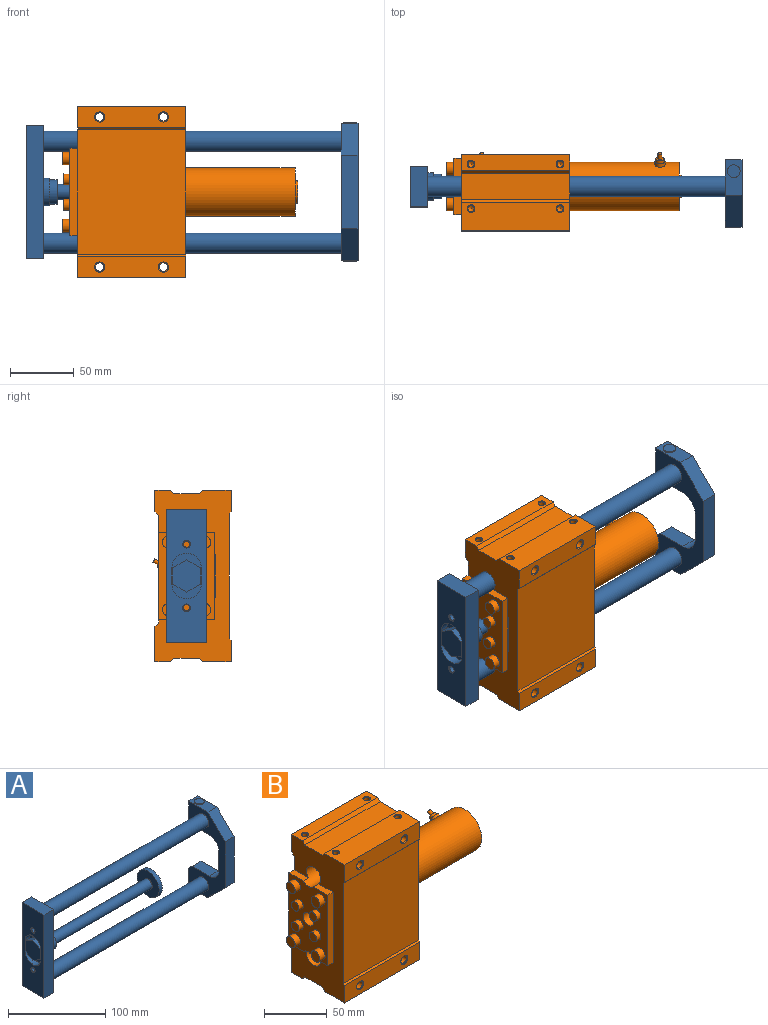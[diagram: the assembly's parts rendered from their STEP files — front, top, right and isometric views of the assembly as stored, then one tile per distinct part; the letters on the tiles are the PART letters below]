
ASSEMBLY  parts=2 mates=1
PART A: 58 faces, bbox 261x53x110 mm
  f0: plane 28x13mm, normal (0,0,1), area 285.5mm2, adj f1,f2,f11,f49,f55
  f1: plane 23x13mm, normal (0,1,0), area 299mm2, adj f0,f2,f49,f53
  f2: plane 108x53mm, normal (1,0,0), area 2468mm2, adj f0,f1,f3,f4,f5,f6,f7,f8
  f3: cylinder r=8mm len=16mm, axis (1,0,0), area 0.5mm2, adj f2,f22
  f4: plane 24x13mm, normal (0,1,0), area 312mm2, adj f2,f49,f51,f52
  f5: plane 25x13mm, normal (0,0,-1), area 325mm2, adj f2,f49,f52,f53
  f6: plane 25x13mm, normal (0,0,1), area 325mm2, adj f2,f49,f50,f51
  f7: plane 23x13mm, normal (0,1,0), area 299mm2, adj f2,f8,f49,f50
  f8: plane 28x13mm, normal (0,0,-1), area 285.5mm2, adj f2,f7,f9,f49,f56
  f9: plane 25x25mm, normal (0,-0.71,-0.71), area 459.6mm2, adj f2,f8,f10,f49
  f10: plane 58x13mm, normal (0,-1,0), area 754mm2, adj f2,f9,f11,f49
  f11: plane 25x25mm, normal (0,-0.71,0.71), area 459.6mm2, adj f0,f2,f10,f49
  f12: plane 32x32mm, normal (1,0,0), area 804.2mm2, adj f13
  f13: cylinder r=16mm len=32mm, axis (-1,0,0), area 502.7mm2, adj f12,f14
  f14: plane 32x32mm, normal (-1,0,0), area 691.2mm2, adj f13,f15
  f15: cylinder r=6mm len=143.23mm, axis (-1,0,0), area 5399.6mm2, adj f14,f16
  f16: plane 19.6x19.6mm, normal (1,0,0), area 188.6mm2, adj f15,f17
  f17: cylinder r=9.8mm len=19.6mm, axis (-1,0,0), area 369.5mm2, adj f16,f18
  f18: plane 22x22mm, normal (1,0,0), area 78.4mm2, adj f17,f19
  f19: cylinder r=11mm len=22mm, axis (-1,0,0), area 311mm2, adj f18,f41
  f20: plane 16x16mm, normal (1,0,0), area 201.1mm2, adj f48
  f21: cylinder r=8mm len=234mm, axis (1,0,0), area 11762.1mm2, adj f41,f49
  f22: plane 16x16mm, normal (1,0,0), area 201.1mm2, adj f3
  f23: cylinder r=8mm len=234mm, axis (1,0,0), area 11762.1mm2, adj f41,f49
  f24: plane 36x23mm, normal (-1,0,0), area 295.3mm2, adj f25,f26,f27,f28,f29,f30,f31,f32
  f25: plane 11x7mm, normal (0,0.5,0.87), area 88.9mm2, adj f24,f26,f30,f47
  f26: plane 12.7x7mm, normal (0,1,0), area 88.9mm2, adj f24,f25,f27,f47
  f27: plane 11x7mm, normal (0,0.5,-0.87), area 88.9mm2, adj f24,f26,f28,f47
  f28: plane 11x7mm, normal (0,-0.5,-0.87), area 88.9mm2, adj f24,f27,f29,f47
  f29: plane 12.7x7mm, normal (0,-1,0), area 88.9mm2, adj f24,f28,f30,f47
  f30: plane 11x7mm, normal (0,-0.5,0.87), area 88.9mm2, adj f24,f25,f29,f47
  f31: cylinder r=11.5mm len=23mm, axis (1,0,0), area 252.9mm2, adj f24,f32,f34,f42
  f32: plane 13x7mm, normal (0,1,0), area 91mm2, adj f24,f31,f33,f42
  f33: cylinder r=11.5mm len=23mm, axis (1,0,0), area 252.9mm2, adj f24,f32,f34,f42
  f34: plane 13x7mm, normal (0,-1,0), area 91mm2, adj f24,f31,f33,f42
  f35: cone r=2.46mm half-angle=45deg, axis (1,0,0), area 13.1mm2, adj f36,f41
  f36: cylinder r=2.46mm len=12.92mm, axis (-1,0,0), area 199.5mm2, adj f35,f37
  f37: cone r=3mm half-angle=45deg, axis (-1,0,0), area 13.1mm2, adj f36,f42
  f38: cone r=2.46mm half-angle=45deg, axis (1,0,0), area 13.1mm2, adj f39,f41
  f39: cylinder r=2.46mm len=12.92mm, axis (-1,0,0), area 199.5mm2, adj f38,f40
  f40: cone r=3mm half-angle=45deg, axis (-1,0,0), area 13.1mm2, adj f39,f42
  f41: plane 105x32mm, normal (1,0,0), area 2521.2mm2, adj f19,f21,f23,f35,f38,f43,f44,f45
  f42: plane 105x32mm, normal (-1,0,0), area 2589mm2, adj f31,f32,f33,f34,f37,f40,f43,f44
  f43: plane 105x14mm, normal (0,1,0), area 1470mm2, adj f41,f42,f44,f46
  f44: plane 32x14mm, normal (0,0,-1), area 448mm2, adj f41,f42,f43,f45
  f45: plane 105x14mm, normal (0,-1,0), area 1470mm2, adj f41,f42,f44,f46
  f46: plane 32x14mm, normal (0,0,1), area 448mm2, adj f41,f42,f43,f45
  f47: plane 25.4x22mm, normal (-1,0,0), area 419.2mm2, adj f25,f26,f27,f28,f29,f30
  f48: cylinder r=8mm len=16mm, axis (1,0,0), area 0.5mm2, adj f2,f20
  f49: plane 108x53mm, normal (-1,0,0), area 2468mm2, adj f0,f1,f4,f5,f6,f7,f8,f9
  f50: plane 13x5mm, normal (0,0.71,0.71), area 91.9mm2, adj f2,f6,f7,f49
  f51: cylinder r=14mm len=14mm, axis (1,0,0), area 285.9mm2, adj f2,f4,f6,f49
  f52: cylinder r=14mm len=14mm, axis (1,0,0), area 285.9mm2, adj f2,f4,f5,f49
  f53: plane 13x5mm, normal (0,0.71,-0.71), area 91.9mm2, adj f1,f2,f5,f49
  f54: plane 10x10mm, normal (0,0,1), area 78.5mm2, adj f55
  f55: cylinder r=5mm len=10mm, axis (0,0,1), area 31.4mm2, adj f0,f54
  f56: cylinder r=5mm len=10mm, axis (0,0,1), area 31.4mm2, adj f8,f57
  f57: plane 10x10mm, normal (0,0,-1), area 78.5mm2, adj f56
PART B: 128 faces, bbox 185x61.5x135 mm
  f0: cone r=866.03mm half-angle=60deg, axis (0,0,-1), area 21.9mm2, adj f1
  f1: cylinder r=2.46mm len=11.46mm, axis (0,0,1), area 177mm2, adj f0,f127
  f2: cone r=2.46mm half-angle=45deg, axis (0,0,-1), area 13.1mm2, adj f43,f103
  f3: cylinder r=19mm len=171mm, axis (1,0,0), area 20162.4mm2, adj f5,f8,f11,f18,f53,f60
  f4: plane 85x12.5mm, normal (0,0,1), area 1006mm2, adj f23,f24,f27,f52,f119,f122
  f5: cylinder r=4.05mm len=8.58mm, axis (0,-0.91,-0.42), area 69.1mm2, adj f3,f59
  f6: plane 18x18mm, normal (1,0,0), area 254.5mm2, adj f7
  f7: cylinder r=9mm len=18mm, axis (1,0,0), area 113.1mm2, adj f6,f18
  f8: cone r=4.28mm half-angle=45deg, axis (0,0.98,-0.17), area 12.2mm2, adj f3,f9
  f9: cylinder r=4.28mm len=9.2mm, axis (0,-0.98,0.17), area 118.9mm2, adj f8,f10
  f10: cone r=866.03mm half-angle=60deg, axis (0,0.98,-0.17), area 66.5mm2, adj f9
  f11: cone r=4.28mm half-angle=45deg, axis (0,0.98,-0.17), area 12.2mm2, adj f3,f12
  f12: cylinder r=4.28mm len=9.2mm, axis (0,-0.98,0.17), area 118.9mm2, adj f11,f13
  f13: cone r=866.03mm half-angle=60deg, axis (0,0.98,-0.17), area 66.5mm2, adj f12
  f14: plane 32x32mm, normal (-1,0,0), area 804.2mm2, adj f15
  f15: cylinder r=16mm len=105mm, axis (-1,0,0), area 10555.8mm2, adj f14,f16
  f16: plane 32x32mm, normal (1,0,0), area 691.2mm2, adj f15,f17
  f17: cylinder r=6mm len=27.73mm, axis (-1,0,0), area 1045.3mm2, adj f16,f62
  f18: plane 38x38mm, normal (1,0,0), area 879.6mm2, adj f3,f7
  f19: plane 69x6mm, normal (0,-1,0), area 414mm2, adj f20,f21,f24,f60,f62
  f20: plane 16.19x6mm, normal (0,0,-1), area 97.1mm2, adj f19,f24,f26,f62
  f21: plane 16.19x6mm, normal (0,0,1), area 97.1mm2, adj f19,f24,f25,f62
  f22: plane 16.19x6mm, normal (0,0,1), area 97.1mm2, adj f24,f25,f29,f62
  f23: plane 135x60mm, normal (1,0,0), area 5183.7mm2, adj f4,f25,f26,f27,f28,f29,f30,f31
  f24: plane 135x60mm, normal (-1,0,0), area 4137.7mm2, adj f4,f19,f20,f21,f22,f25,f26,f27
  f25: cylinder r=8mm len=91mm, axis (1,0,0), area 4350.6mm2, adj f21,f22,f23,f24,f62
  f26: cylinder r=8mm len=91mm, axis (1,0,0), area 4350.6mm2, adj f20,f23,f24,f61,f62
  f27: plane 85x17mm, normal (0,1,0), area 1254.9mm2, adj f4,f23,f24,f28,f84,f90
  f28: plane 85x3mm, normal (0,0.71,-0.71), area 360.6mm2, adj f23,f24,f27,f29
  f29: plane 91x84.5mm, normal (0,1,0), area 3006.5mm2, adj f22,f23,f24,f28,f30,f36,f37,f60
  f30: plane 85x5mm, normal (0,0.71,-0.71), area 601mm2, adj f23,f29,f31,f60
  f31: plane 85x33.5mm, normal (0,0,-1), area 2847.5mm2, adj f23,f30,f32,f60
  f32: cylinder r=6mm len=85mm, axis (1,0,0), area 801.1mm2, adj f23,f24,f31,f33,f60
  f33: plane 85x32mm, normal (0,1,0), area 2720mm2, adj f23,f24,f32,f34
  f34: cylinder r=6mm len=85mm, axis (1,0,0), area 801.1mm2, adj f23,f24,f33,f35,f60
  f35: plane 85x33.5mm, normal (0,0,1), area 2847.5mm2, adj f23,f34,f36,f60
  f36: plane 85x5mm, normal (0,0.71,0.71), area 601mm2, adj f23,f29,f35,f60
  f37: plane 85x3mm, normal (0,0.71,0.71), area 360.6mm2, adj f23,f24,f29,f38
  f38: plane 85x27.5mm, normal (0,1,0), area 2147.4mm2, adj f23,f24,f37,f39,f96,f102
  f39: plane 85x12.5mm, normal (0,0,-1), area 1006mm2, adj f23,f24,f38,f40,f105,f108
  f40: plane 85x3mm, normal (0,-0.77,-0.64), area 332.9mm2, adj f23,f24,f39,f41
  f41: plane 85x19.97mm, normal (0,0,-1), area 1697.1mm2, adj f23,f24,f40,f42
  f42: plane 85x3mm, normal (0,0.77,-0.64), area 332.9mm2, adj f23,f24,f41,f43
  f43: plane 85x22.5mm, normal (0,0,-1), area 1856mm2, adj f2,f23,f24,f42,f44,f127
  f44: plane 85x17mm, normal (0,-1,0), area 1344.5mm2, adj f23,f24,f43,f45,f91,f97
  f45: plane 85x1.5mm, normal (0,-0.71,0.71), area 180.3mm2, adj f23,f24,f44,f46
  f46: plane 98x85mm, normal (0,-1,0), area 8330mm2, adj f23,f24,f45,f47
  f47: plane 85x1.5mm, normal (0,-0.71,-0.71), area 180.3mm2, adj f23,f24,f46,f48
  f48: plane 85x17mm, normal (0,-1,0), area 1344.5mm2, adj f23,f24,f47,f49,f79,f85
  f49: plane 85x22.5mm, normal (0,0,1), area 1856mm2, adj f23,f24,f48,f50,f113,f116
  f50: plane 85x3mm, normal (0,0.77,0.64), area 332.9mm2, adj f23,f24,f49,f51
  f51: plane 85x19.97mm, normal (0,0,1), area 1697.1mm2, adj f23,f24,f50,f52
  f52: plane 85x3mm, normal (0,-0.77,0.64), area 332.9mm2, adj f4,f23,f24,f51
  f53: cylinder r=4.05mm len=8.58mm, axis (0,-0.91,-0.42), area 69.1mm2, adj f3,f54
  f54: plane 8.1x7.34mm, normal (0,0.91,0.42), area 14.1mm2, adj f53,f126
  f55: plane 3.2x2.9mm, normal (0,0.91,0.42), area 8mm2, adj f56
  f56: cylinder r=1.6mm len=5.52mm, axis (0,-0.91,-0.42), area 46.2mm2, adj f55,f57
  f57: plane 6.9x6.25mm, normal (0,0.91,0.42), area 29.4mm2, adj f56,f58
  f58: cylinder r=3.45mm len=7.27mm, axis (0,-0.91,-0.42), area 52mm2, adj f57,f59
  f59: plane 8.1x7.34mm, normal (0,0.91,0.42), area 14.1mm2, adj f5,f58
  f60: plane 54x44mm, normal (1,0,0), area 815.8mm2, adj f3,f19,f29,f30,f31,f32,f34,f35
  f61: plane 16.19x6mm, normal (0,0,-1), area 97.1mm2, adj f24,f26,f29,f62
  f62: plane 69x44mm, normal (-1,0,0), area 2341.6mm2, adj f17,f19,f20,f21,f22,f25,f26,f29
  f63: plane 10x10mm, normal (-1,0,0), area 78.5mm2, adj f66
  f64: cylinder r=5mm len=10mm, axis (-1,0,0), area 188.5mm2, adj f62,f65
  f65: plane 10x10mm, normal (-1,0,0), area 78.5mm2, adj f64
  f66: cylinder r=5mm len=10mm, axis (-1,0,0), area 188.5mm2, adj f62,f63
  f67: plane 10x10mm, normal (-1,0,0), area 78.5mm2, adj f68
  f68: cylinder r=5mm len=10mm, axis (-1,0,0), area 188.5mm2, adj f62,f67
  f69: plane 10x10mm, normal (-1,0,0), area 78.5mm2, adj f70
  f70: cylinder r=5mm len=10mm, axis (-1,0,0), area 188.5mm2, adj f62,f69
  f71: plane 8.5x8.5mm, normal (-1,0,0), area 56.7mm2, adj f72
  f72: cylinder r=4.25mm len=8.5mm, axis (-1,0,0), area 133.5mm2, adj f62,f71
  f73: plane 8.5x8.5mm, normal (-1,0,0), area 56.7mm2, adj f74
  f74: cylinder r=4.25mm len=8.5mm, axis (-1,0,0), area 133.5mm2, adj f62,f73
  f75: plane 8.5x8.5mm, normal (-1,0,0), area 56.7mm2, adj f76
  f76: cylinder r=4.25mm len=8.5mm, axis (-1,0,0), area 133.5mm2, adj f62,f75
  f77: plane 8.5x8.5mm, normal (-1,0,0), area 56.7mm2, adj f78
  f78: cylinder r=4.25mm len=8.5mm, axis (-1,0,0), area 133.5mm2, adj f62,f77
  f79: cone r=4mm half-angle=45deg, axis (0,-1,0), area 22mm2, adj f48,f80
  f80: cylinder r=3.32mm len=13.32mm, axis (0,-1,0), area 278.2mm2, adj f79,f81
  f81: plane 6.8x6.8mm, normal (0,1,0), area 1.6mm2, adj f80,f82
  f82: cylinder r=3.4mm len=38mm, axis (0,-1,0), area 811.8mm2, adj f81,f83
  f83: plane 11x11mm, normal (0,1,0), area 58.7mm2, adj f82,f84
  f84: cylinder r=5.5mm len=11mm, axis (0,-1,0), area 276.5mm2, adj f27,f83
  f85: cone r=4mm half-angle=45deg, axis (0,-1,0), area 22mm2, adj f48,f86
  f86: cylinder r=3.32mm len=13.32mm, axis (0,-1,0), area 278.2mm2, adj f85,f87
  f87: plane 6.8x6.8mm, normal (0,1,0), area 1.6mm2, adj f86,f88
  f88: cylinder r=3.4mm len=38mm, axis (0,-1,0), area 811.8mm2, adj f87,f89
  f89: plane 11x11mm, normal (0,1,0), area 58.7mm2, adj f88,f90
  f90: cylinder r=5.5mm len=11mm, axis (0,-1,0), area 276.5mm2, adj f27,f89
  f91: cone r=4mm half-angle=45deg, axis (0,-1,0), area 22mm2, adj f44,f92
  f92: cylinder r=3.32mm len=13.32mm, axis (0,-1,0), area 278.2mm2, adj f91,f93
  f93: plane 6.8x6.8mm, normal (0,1,0), area 1.6mm2, adj f92,f94
  f94: cylinder r=3.4mm len=38mm, axis (0,-1,0), area 811.8mm2, adj f93,f95
  f95: plane 11x11mm, normal (0,1,0), area 58.7mm2, adj f94,f96
  f96: cylinder r=5.5mm len=11mm, axis (0,-1,0), area 276.5mm2, adj f38,f95
  f97: cone r=4mm half-angle=45deg, axis (0,-1,0), area 22mm2, adj f44,f98
  f98: cylinder r=3.32mm len=13.32mm, axis (0,-1,0), area 278.2mm2, adj f97,f99
  f99: plane 6.8x6.8mm, normal (0,1,0), area 1.6mm2, adj f98,f100
  f100: cylinder r=3.4mm len=38mm, axis (0,-1,0), area 811.8mm2, adj f99,f101
  f101: plane 11x11mm, normal (0,1,0), area 58.7mm2, adj f100,f102
  f102: cylinder r=5.5mm len=11mm, axis (0,-1,0), area 276.5mm2, adj f38,f101
  f103: cylinder r=2.46mm len=11.46mm, axis (0,0,1), area 177mm2, adj f2,f104
  f104: cone r=866.03mm half-angle=60deg, axis (0,0,-1), area 21.9mm2, adj f103
  f105: cone r=2.46mm half-angle=45deg, axis (0,0,-1), area 13.1mm2, adj f39,f106
  f106: cylinder r=2.46mm len=11.46mm, axis (0,0,1), area 177mm2, adj f105,f107
  f107: cone r=866.03mm half-angle=60deg, axis (0,0,-1), area 21.9mm2, adj f106
  f108: cone r=2.46mm half-angle=45deg, axis (0,0,-1), area 13.1mm2, adj f39,f109
  f109: cylinder r=2.46mm len=11.46mm, axis (0,0,1), area 177mm2, adj f108,f110
  f110: cone r=866.03mm half-angle=60deg, axis (0,0,-1), area 21.9mm2, adj f109
  f111: cone r=2.46mm half-angle=60deg, axis (0,0,1), area 21.9mm2, adj f112
  f112: cylinder r=2.46mm len=11.46mm, axis (0,0,1), area 177mm2, adj f111,f113
  f113: cone r=3mm half-angle=45deg, axis (0,0,1), area 13.1mm2, adj f49,f112
  f114: cone r=2.46mm half-angle=60deg, axis (0,0,1), area 21.9mm2, adj f115
  f115: cylinder r=2.46mm len=11.46mm, axis (0,0,1), area 177mm2, adj f114,f116
  f116: cone r=3mm half-angle=45deg, axis (0,0,1), area 13.1mm2, adj f49,f115
  f117: cone r=2.46mm half-angle=60deg, axis (0,0,1), area 21.9mm2, adj f118
  f118: cylinder r=2.46mm len=11.46mm, axis (0,0,1), area 177mm2, adj f117,f119
  f119: cone r=3mm half-angle=45deg, axis (0,0,1), area 13.1mm2, adj f4,f118
  f120: cone r=2.46mm half-angle=60deg, axis (0,0,1), area 21.9mm2, adj f121
  f121: cylinder r=2.46mm len=11.46mm, axis (0,0,1), area 177mm2, adj f120,f122
  f122: cone r=3mm half-angle=45deg, axis (0,0,1), area 13.1mm2, adj f4,f121
  f123: plane 3.2x2.9mm, normal (0,0.91,0.42), area 8mm2, adj f124
  f124: cylinder r=1.6mm len=5.52mm, axis (0,-0.91,-0.42), area 46.2mm2, adj f123,f125
  f125: plane 6.9x6.25mm, normal (0,0.91,0.42), area 29.4mm2, adj f124,f126
  f126: cylinder r=3.45mm len=7.27mm, axis (0,-0.91,-0.42), area 52mm2, adj f54,f125
  f127: cone r=2.46mm half-angle=45deg, axis (0,0,-1), area 13.1mm2, adj f1,f43
PLACE A t=(5.5,78.99,0)mm
PLACE B t=(0,78.99,0)mm
MATE slider A.f13 <-> B.f3  axis (-1,0,0) through (-16,78.99,0)mm
